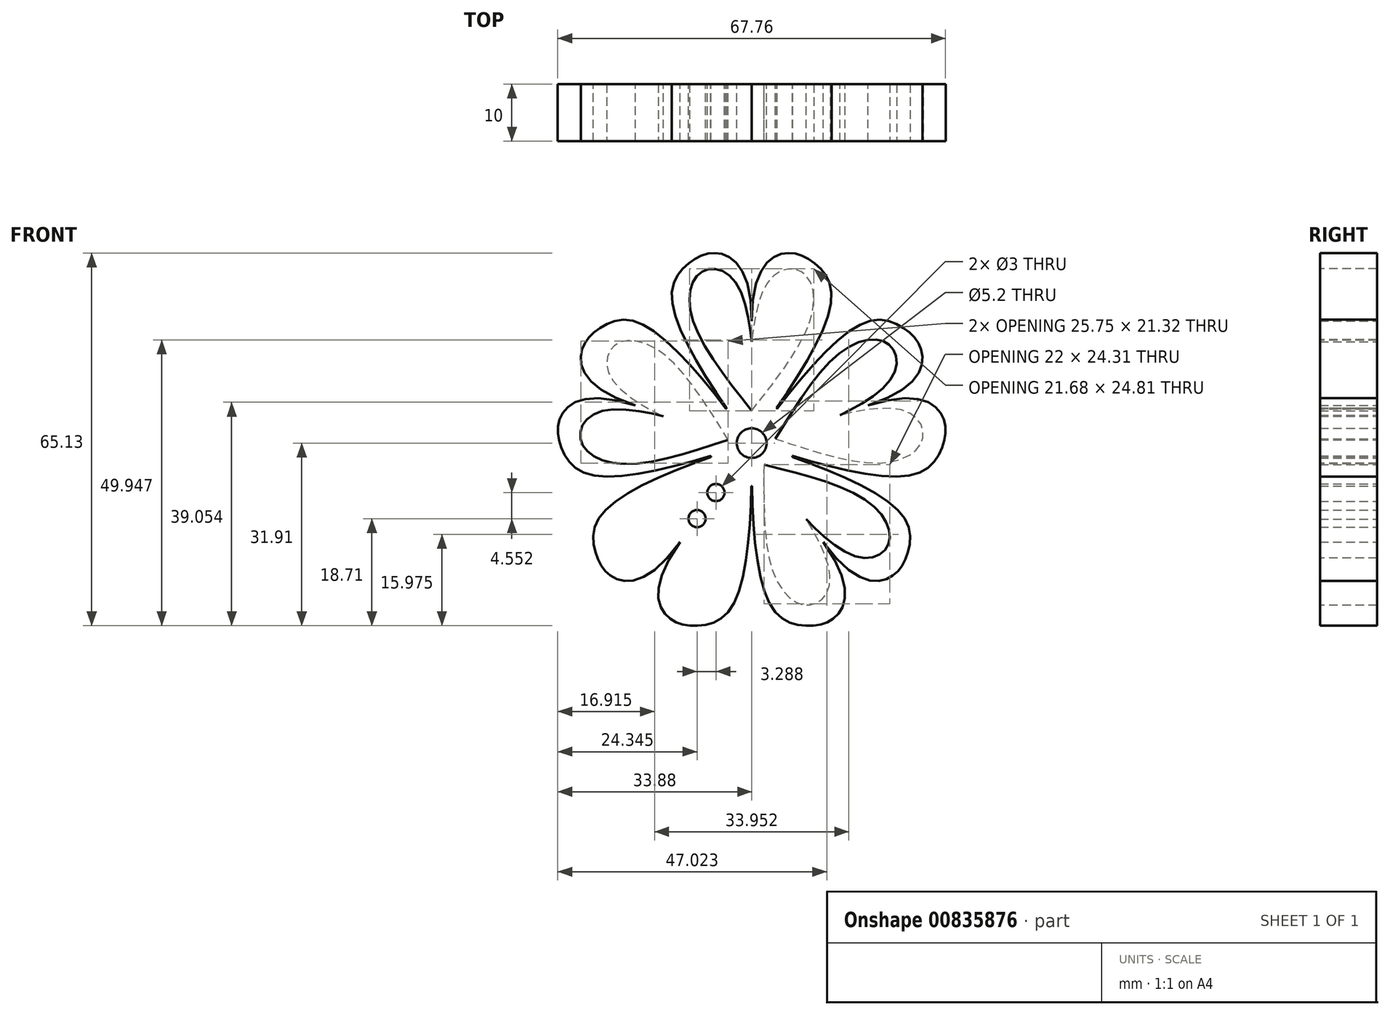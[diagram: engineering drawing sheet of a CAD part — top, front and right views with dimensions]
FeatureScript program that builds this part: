
annotation { "Feature Type Name" : "Feature", "Feature Type Description" : "" }
export const myFeature = defineFeature(function(context is Context, id is Id, definition is map)
    precondition{}
    {
        {
            var Q0;
            Q0=qCreatedBy(makeId("Front.planeOp"),FACE);
            var sketch = newSketch(context, id + "F0", { "sketchPlane" : qUnion([Q0])});
            skFitSpline(sketch, "E0", {"points": [v(0, 0) * mm, v(-13.95, 25.24) * mm, v(-10.68, 31.65) * mm, v(-6, 33.2) * mm, v(0, 21.33) * mm], "startDerivative": vector(-42.85, 58.9) * mm, "endDerivative": vector(0, -104.89) * mm});
            skFitSpline(sketch, "E1.MirrorCS", {"points": [v(0, 0) * mm, v(13.95, 25.24) * mm, v(10.68, 31.65) * mm, v(6, 33.2) * mm, v(0, 21.33) * mm], "startDerivative": vector(42.85, 58.9) * mm, "endDerivative": vector(0, -104.89) * mm});
            skLineSegment(sketch, "E2", {"start": v(0, 0) * mm, "end": v(37.75, 51.88) * mm});
            skFitSpline(sketch, "E3.MirrorCS", {"points": [v(0, 0) * mm, v(19.72, 21.04) * mm, v(26.82, 19.9) * mm, v(29.74, 15.93) * mm, v(20.3, 6.56) * mm], "startDerivative": vector(42.85, 58.9) * mm, "endDerivative": vector(-99.8, -32.27) * mm});
            skFitSpline(sketch, "E4.MirrorCS", {"points": [v(0, 0) * mm, v(28.3, -5.5) * mm, v(33.4, -0.43) * mm, v(33.43, 4.5) * mm, v(20.3, 6.56) * mm], "startDerivative": vector(69.23, -22.65) * mm, "endDerivative": vector(-99.8, -32.27) * mm});
            skLineSegment(sketch, "E5", {"start": v(0, 0) * mm, "end": v(5.51, -1.8) * mm});
            skFitSpline(sketch, "E6.MirrorCS", {"points": [v(0, 0) * mm, v(26.09, -12.3) * mm, v(27.2, -19.4) * mm, v(24.3, -23.4) * mm, v(12.5, -17.3) * mm], "startDerivative": vector(69.23, -22.65) * mm, "endDerivative": vector(-61.42, 85.03) * mm});
            skFitSpline(sketch, "E7.MirrorCS", {"points": [v(0, 0) * mm, v(3.47, -28.63) * mm, v(9.87, -31.9) * mm, v(14.57, -30.42) * mm, v(12.5, -17.3) * mm], "startDerivative": vector(-0.25, -72.84) * mm, "endDerivative": vector(-61.42, 85.03) * mm});
            skFitSpline(sketch, "E8.MirrorCS", {"points": [v(0, 0) * mm, v(-13.95, 25.24) * mm, v(-10.68, 31.65) * mm, v(-6, 33.2) * mm, v(0, 21.33) * mm], "startDerivative": vector(-42.85, 58.9) * mm, "endDerivative": vector(0, -104.89) * mm});
            skFitSpline(sketch, "E9.MirrorCS", {"points": [v(0, 0) * mm, v(-19.72, 21.04) * mm, v(-26.82, 19.9) * mm, v(-29.74, 15.93) * mm, v(-20.3, 6.56) * mm], "startDerivative": vector(-42.85, 58.9) * mm, "endDerivative": vector(99.8, -32.27) * mm});
            skFitSpline(sketch, "E10.MirrorCS", {"points": [v(0, 0) * mm, v(-28.3, -5.5) * mm, v(-33.4, -0.43) * mm, v(-33.43, 4.5) * mm, v(-20.3, 6.56) * mm], "startDerivative": vector(-69.23, -22.65) * mm, "endDerivative": vector(99.8, -32.27) * mm});
            skFitSpline(sketch, "E11.MirrorCS", {"points": [v(0, 0) * mm, v(-26.09, -12.3) * mm, v(-27.2, -19.4) * mm, v(-24.3, -23.4) * mm, v(-12.5, -17.3) * mm], "startDerivative": vector(-69.23, -22.65) * mm, "endDerivative": vector(61.42, 85.03) * mm});
            skFitSpline(sketch, "E12.MirrorCS", {"points": [v(0, 0) * mm, v(-3.47, -28.63) * mm, v(-9.87, -31.9) * mm, v(-14.57, -30.42) * mm, v(-12.5, -17.3) * mm], "startDerivative": vector(0.25, -72.84) * mm, "endDerivative": vector(61.42, 85.03) * mm});
            skSolve(sketch);
        }
        {
            var Q0;
            Q0 = qSketchRegion(id + "F0", true);
            extrude(context, id + "F1", {"entities" : qUnion([Q0]), "endBound" : BoundingType.SYMMETRIC, "depth" : 10 * mm, "offsetDistance" : 25 * mm});
        }
        {
            var Q0;
            Q0=qCreatedBy(makeId("Front.planeOp"),FACE);
            var sketch = newSketch(context, id + "F2", { "sketchPlane" : qUnion([Q0])});
            skCircle(sketch, "E13", {"center": v(0, 0) * mm, "radius": 7.5 * mm});
            skSolve(sketch);
        }
        {
            var Q0;
            Q0 = qSketchRegion(id + "F2", true);
            extrude(context, id + "F3", {"entities" : qUnion([Q0]), "operationType" : NewBodyOperationType.ADD, "endBound" : BoundingType.SYMMETRIC, "depth" : 10 * mm, "offsetDistance" : 25 * mm});
        }
        {
            var Q0;
            Q0=qCreatedBy(makeId("Front.planeOp"),FACE);
            var sketch = newSketch(context, id + "F4", { "sketchPlane" : qUnion([Q0])});
            skFitSpline(sketch, "E14", {"points": [v(0, 5.63) * mm, v(-10.2, 21.31) * mm, v(-10.02, 28.58) * mm, v(-7.01, 30.45) * mm, v(-2.64, 27.83) * mm, v(0.1, 16.52) * mm], "startDerivative": vector(-40.13, 51.07) * mm, "endDerivative": vector(2.42, -38.33) * mm});
            skFitSpline(sketch, "E15.MirrorCS", {"points": [v(0, 5.63) * mm, v(10.2, 21.31) * mm, v(10.02, 28.58) * mm, v(7.01, 30.45) * mm, v(2.64, 27.83) * mm, v(-0.1, 16.52) * mm], "startDerivative": vector(40.13, 51.07) * mm, "endDerivative": vector(-2.42, -38.33) * mm});
            skFitSpline(sketch, "E16", {"points": [v(4.11, 0.74) * mm, v(15.35, 15.7) * mm, v(22.25, 18) * mm, v(25.04, 15.82) * mm, v(24.07, 10.82) * mm, v(14.38, 4.38) * mm], "startDerivative": vector(34.26, 55.18) * mm, "endDerivative": vector(-35.2, -15.38) * mm});
            skFitSpline(sketch, "E17.MirrorCS", {"points": [v(4.11, 0.74) * mm, v(22.34, -3.49) * mm, v(29.1, -0.82) * mm, v(29.83, 2.64) * mm, v(25.88, 5.85) * mm, v(14.32, 4.56) * mm], "startDerivative": vector(61.71, -20.24) * mm, "endDerivative": vector(-36.85, -10.84) * mm});
            skFitSpline(sketch, "E18", {"points": [v(2.14, -3.78) * mm, v(19.82, -9.9) * mm, v(24.13, -15.77) * mm, v(22.9, -19.08) * mm, v(17.85, -19.7) * mm, v(8.75, -12.44) * mm], "startDerivative": vector(63.02, -15.73) * mm, "endDerivative": vector(-25.42, 28.8) * mm});
            skFitSpline(sketch, "E19.MirrorCS", {"points": [v(2.14, -3.78) * mm, v(3.7, -22.42) * mm, v(8.3, -28.05) * mm, v(11.82, -27.68) * mm, v(13.67, -22.94) * mm, v(8.9, -12.33) * mm], "startDerivative": vector(-0.38, -64.95) * mm, "endDerivative": vector(-21.6, 31.76) * mm});
            skFitSpline(sketch, "E20", {"points": [v(-4.1, 0.57) * mm, v(-22.32, -3.66) * mm, v(-29.08, -1) * mm, v(-29.81, 2.47) * mm, v(-25.86, 5.68) * mm, v(-14.3, 4.38) * mm], "startDerivative": vector(-61.71, -20.24) * mm, "endDerivative": vector(36.85, -10.84) * mm});
            skFitSpline(sketch, "E21.MirrorCS", {"points": [v(-4.1, 0.57) * mm, v(-15.33, 15.52) * mm, v(-22.23, 17.83) * mm, v(-25.01, 15.64) * mm, v(-24.05, 10.64) * mm, v(-14.36, 4.2) * mm], "startDerivative": vector(-34.26, 55.18) * mm, "endDerivative": vector(35.2, -15.38) * mm});
            skSolve(sketch);
        }
        {
            var Q0;
            Q0 = qSketchRegion(id + "F4", true);
            extrude(context, id + "F5", {"entities" : qUnion([Q0]), "operationType" : NewBodyOperationType.REMOVE, "endBound" : BoundingType.SYMMETRIC, "depth" : 25 * mm, "offsetDistance" : 25 * mm});
        }
        {
            var Q0;
            Q0=qCreatedBy(makeId("Front.planeOp"),FACE);
            var sketch = newSketch(context, id + "F6", { "sketchPlane" : qUnion([Q0])});
            skPoint(sketch, "E22", {"position": v(-9.54, -13.2) * mm});
            skCircle(sketch, "E23", {"center": v(-9.54, -13.2) * mm, "radius": 1.5 * mm});
            skCircle(sketch, "E24", {"center": v(0, 0) * mm, "radius": 2.6 * mm});
            skPoint(sketch, "E25", {"position": v(-6.25, -8.65) * mm});
            skCircle(sketch, "E26", {"center": v(-6.25, -8.65) * mm, "radius": 1.5 * mm});
            skSolve(sketch);
        }
        {
            var Q0;
            Q0 = qSketchRegion(id + "F6", true);
            extrude(context, id + "F7", {"entities" : qUnion([Q0]), "operationType" : NewBodyOperationType.REMOVE, "endBound" : BoundingType.SYMMETRIC, "depth" : 20 * mm, "offsetDistance" : 25 * mm});
        }
    });
